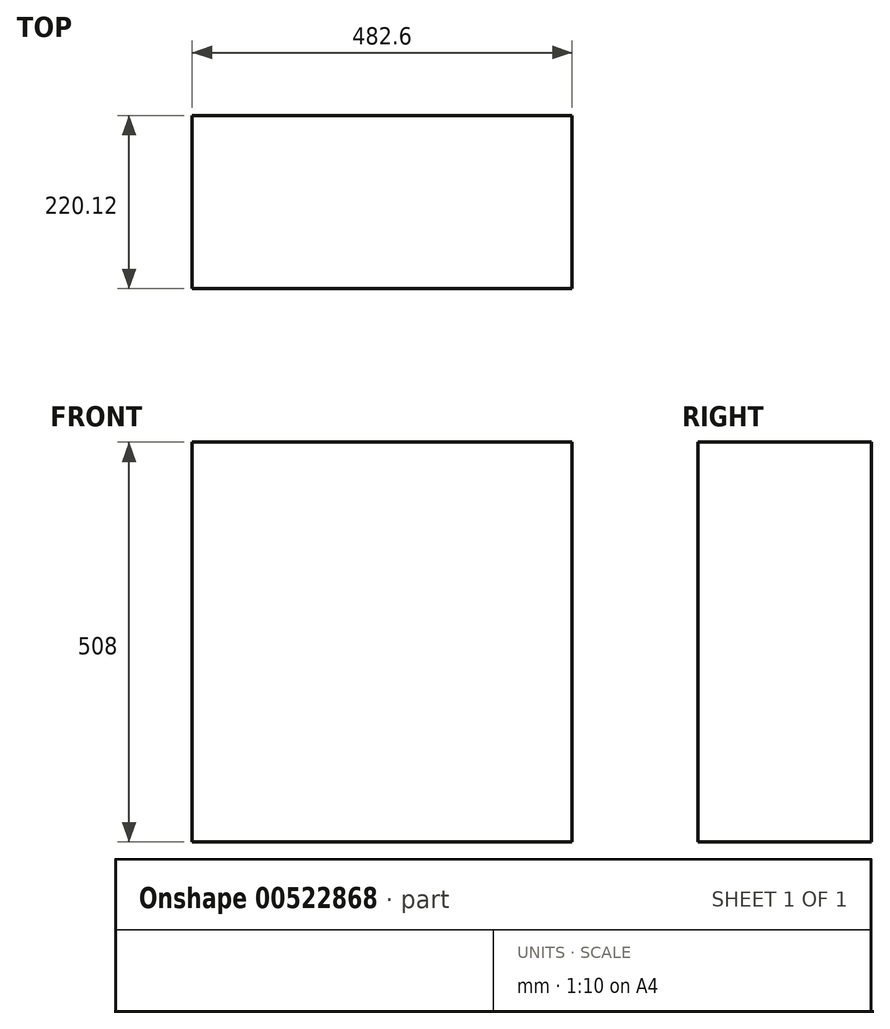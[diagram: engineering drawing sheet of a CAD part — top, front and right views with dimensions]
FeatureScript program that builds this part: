
annotation { "Feature Type Name" : "Feature", "Feature Type Description" : "" }
export const myFeature = defineFeature(function(context is Context, id is Id, definition is map)
    precondition{}
    {
        {
            var Q0;
            Q0=qCreatedBy(makeId("Top.planeOp"),FACE);
            var sketch = newSketch(context, id + "F0", { "sketchPlane" : qUnion([Q0])});
            skLineSegment(sketch, "E0.bottom", {"start": v(-239.5, -110.06) * mm, "end": v(243.1, -110.06) * mm});
            skLineSegment(sketch, "E0.top", {"start": v(-239.5, 110.06) * mm, "end": v(243.1, 110.06) * mm});
            skLineSegment(sketch, "E0.left", {"start": v(-239.5, -110.06) * mm, "end": v(-239.5, 110.06) * mm});
            skLineSegment(sketch, "E0.right", {"start": v(243.1, -110.06) * mm, "end": v(243.1, 110.06) * mm});
            skPoint(sketch, "E0.middle", {"position": v(1.8, 0) * mm});
            skSolve(sketch);
        }
        {
            var Q0;
            Q0 = qSketchRegion(id + "F0", true);
            extrude(context, id + "F1", {"entities" : qUnion([Q0]), "depth" : 508 * mm, "offsetDistance" : 25 * mm});
        }
    });
